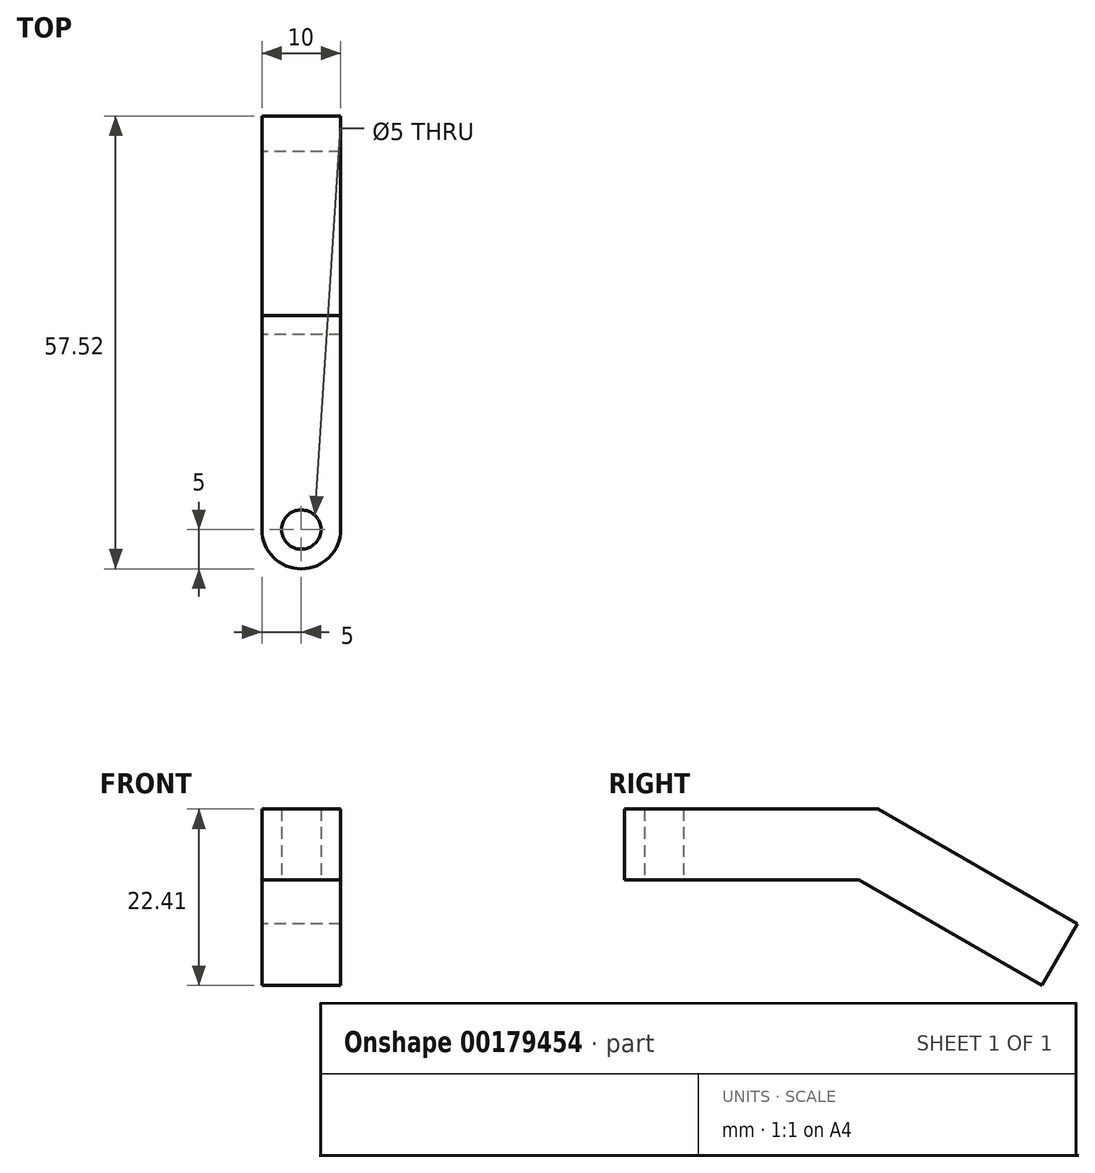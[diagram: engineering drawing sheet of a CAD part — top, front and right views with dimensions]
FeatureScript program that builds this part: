
annotation { "Feature Type Name" : "Feature", "Feature Type Description" : "" }
export const myFeature = defineFeature(function(context is Context, id is Id, definition is map)
    precondition{}
    {
        {
            var Q0;
            Q0=qCreatedBy(makeId("Right.planeOp"),FACE);
            var sketch = newSketch(context, id + "F0", { "sketchPlane" : qUnion([Q0])});
            skLineSegment(sketch, "E0", {"start": v(-24.9, 22.04) * mm, "end": v(2.31, 22.04) * mm});
            skLineSegment(sketch, "E1", {"start": v(2.31, 22.04) * mm, "end": v(27.63, 7.43) * mm});
            skLineSegment(sketch, "E2", {"start": v(27.63, 7.43) * mm, "end": v(23.13, -0.37) * mm});
            skLineSegment(sketch, "E3", {"start": v(23.13, -0.37) * mm, "end": v(-0.1, 13.04) * mm});
            skLineSegment(sketch, "E4", {"start": v(-0.1, 13.04) * mm, "end": v(-24.9, 13.04) * mm});
            skLineSegment(sketch, "E5", {"start": v(-24.9, 13.04) * mm, "end": v(-24.9, 22.04) * mm});
            skSolve(sketch);
        }
        {
            var Q0;
            Q0=makeQuery(id+"F0.imprint","IMPRINT",FACE,{"disambiguationData":[TD([[makeQuery(id+"F0.imprint","IMPRINT",EDGE,{"derivedFrom":sQuery(id+"F0.wireOp",EDGE,"E0")}),-1.0]])]});
            extrude(context, id + "F1", {"entities" : qUnion([Q0]), "depth" : 10 * mm, "offsetDistance" : 25 * mm});
        }
        {
            var Q0;
            Q0=makeQuery(id+"F1.opExtrude","SWEPT_FACE",FACE,{"disambiguationData":[OSD([sQuery(id+"F0.wireOp",EDGE,"E4")])]});
            var sketch = newSketch(context, id + "F2", { "sketchPlane" : qUnion([Q0])});
            skCircle(sketch, "E6", {"center": v(5, 24.9) * mm, "radius": 5 * mm});
            skSolve(sketch);
        }
        {
            var Q0;
            {var subQ1=sQuery(id+"F0.wireOp",EDGE,"E4");var subQ2=makeQuery(id+"F1.opExtrude","SWEPT_EDGE",EDGE,{"disambiguationData":[OSD([subQ1,sQuery(id+"F0.wireOp",EDGE,"E5")])]});Q0=makeQuery(id+"F2.imprint","IMPRINT",FACE,{"disambiguationData":[TD([[makeQuery(id+"F2.imprint","IMPRINT",EDGE,{"derivedFrom":subQ2}),-1.0]])]});}
            extrude(context, id + "F3", {"entities" : qUnion([Q0]), "operationType" : NewBodyOperationType.ADD, "oppositeDirection" : true, "depth" : 9 * mm, "offsetDistance" : 25 * mm});
        }
        {
            var Q0;
            {var subQ0=sQuery(id+"F0.wireOp",EDGE,"E4");Q0=makeQuery(id+"F3.boolean.opBoolean","MERGE",FACE,{"derivedFrom":[makeQuery(id+"F1.opExtrude","SWEPT_FACE",FACE,{"disambiguationData":[OSD([subQ0])]}),makeQuery(id+"F3.opExtrude","CAP_FACE",FACE,{"disambiguationData":[OSD([subQ0,sQuery(id+"F0.wireOp",EDGE,"E5"),sQuery(id+"F2.wireOp",EDGE,"E6")])],"isStart":true})]});}
            var sketch = newSketch(context, id + "F4", { "sketchPlane" : qUnion([Q0])});
            skCircle(sketch, "E7", {"center": v(5, 24.9) * mm, "radius": 2.5 * mm});
            skSolve(sketch);
        }
        {
            var Q0;
            Q0=makeQuery(id+"F4.imprint","IMPRINT",FACE,{"disambiguationData":[TD([[makeQuery(id+"F4.imprint","IMPRINT",EDGE,{"derivedFrom":sQuery(id+"F4.wireOp",EDGE,"E7")}),1.0]])]});
            extrude(context, id + "F5", {"entities" : qUnion([Q0]), "operationType" : NewBodyOperationType.REMOVE, "oppositeDirection" : true, "depth" : 9 * mm, "offsetDistance" : 25 * mm});
        }
    });
